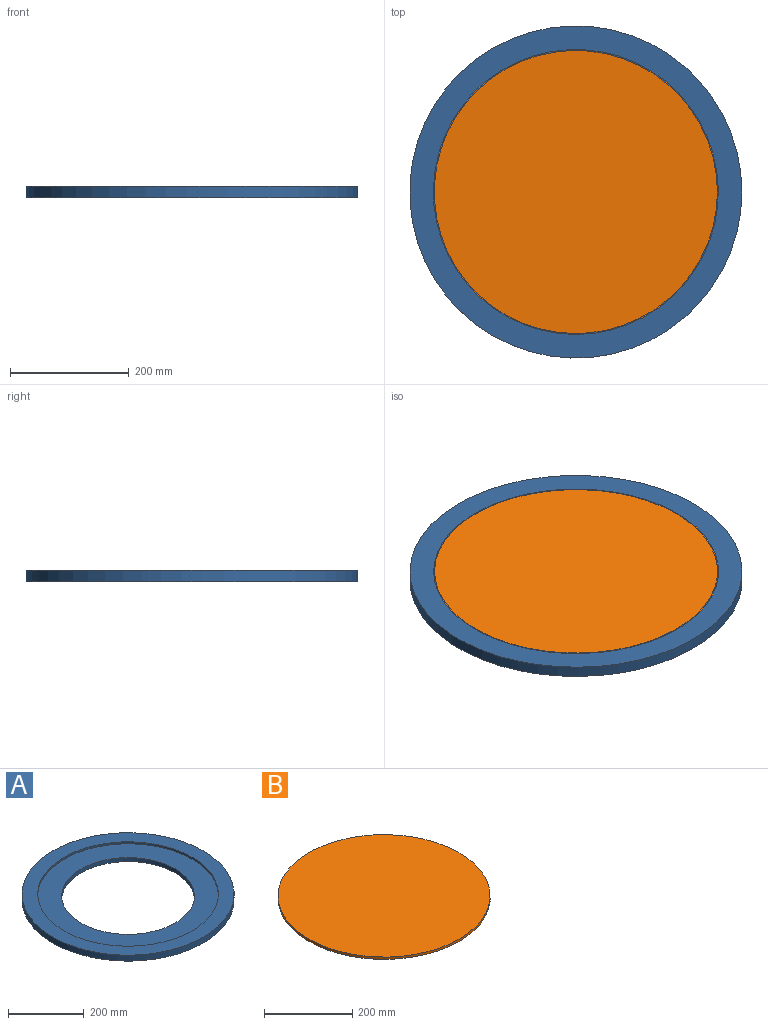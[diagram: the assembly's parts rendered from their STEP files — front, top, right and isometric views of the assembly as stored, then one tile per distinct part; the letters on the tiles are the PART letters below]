
ASSEMBLY  parts=2 mates=1
PART A: 6 faces, bbox 558.8x558.8x19.1 mm
  f0: cylinder r=279.4mm len=558.8mm, axis (0,0,-1), area 33442.7mm2, adj f1,f2
  f1: plane 558.8x558.8mm, normal (0,0,1), area 67107.1mm2, adj f0,f3
  f2: plane 558.8x558.8mm, normal (0,0,-1), area 149035.1mm2, adj f0,f5
  f3: cylinder r=238.12mm len=476.25mm, axis (0,0,1), area 9500.8mm2, adj f1,f4
  f4: plane 476.25x476.25mm, normal (0,0,1), area 81928.1mm2, adj f3,f5
  f5: cylinder r=175mm len=350mm, axis (0,0,1), area 13964.4mm2, adj f2,f4
PART B: 3 faces, bbox 479.4x479.4x6.4 mm
  f0: cylinder r=239.71mm len=479.43mm, axis (0,0,-1), area 9564.1mm2, adj f1,f2
  f1: plane 479.43x479.43mm, normal (0,0,1), area 180522.5mm2, adj f0
  f2: plane 479.43x479.43mm, normal (0,0,-1), area 180522.5mm2, adj f0
PLACE A t=(-205.12,-64.5,68.2)mm
PLACE B t=(-205.12,-64.5,80.9)mm
MATE planar A.f3 <-> B.f0  axis (0,0,1) through (-205.12,-64.5,80.9)mm
